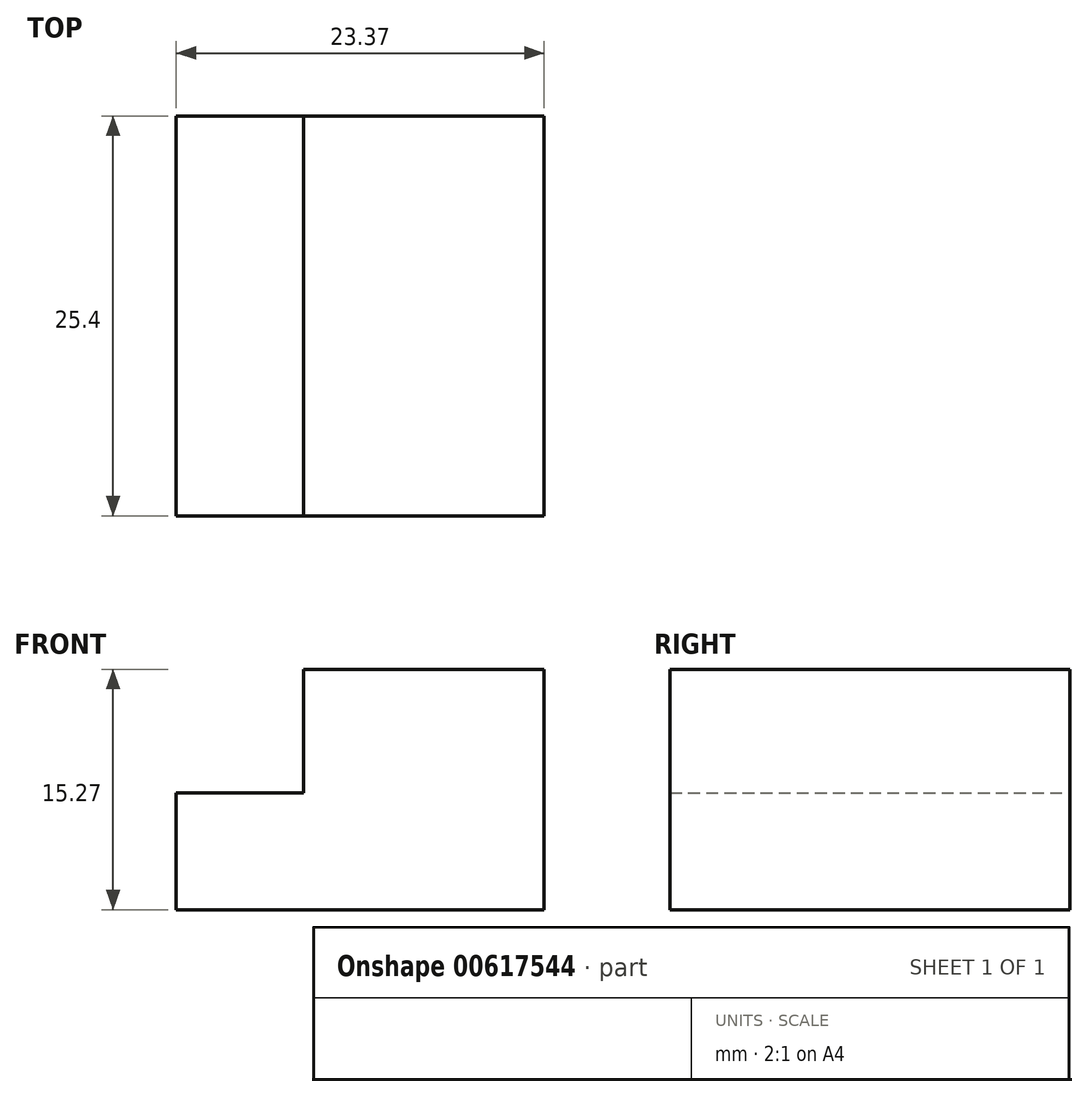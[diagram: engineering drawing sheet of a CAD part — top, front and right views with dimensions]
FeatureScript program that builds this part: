
annotation { "Feature Type Name" : "Feature", "Feature Type Description" : "" }
export const myFeature = defineFeature(function(context is Context, id is Id, definition is map)
    precondition{}
    {
        {
            var Q0;
            Q0=qCreatedBy(makeId("Front.planeOp"),FACE);
            var sketch = newSketch(context, id + "F0", { "sketchPlane" : qUnion([Q0])});
            skLineSegment(sketch, "E0", {"start": v(23.37, 0) * mm, "end": v(23.37, 15.27) * mm});
            skLineSegment(sketch, "E1", {"start": v(23.37, 15.27) * mm, "end": v(8.1, 15.27) * mm});
            skLineSegment(sketch, "E2", {"start": v(8.1, 15.27) * mm, "end": v(8.1, 7.4) * mm});
            skLineSegment(sketch, "E3", {"start": v(8.1, 7.4) * mm, "end": v(0, 7.4) * mm});
            skLineSegment(sketch, "E4", {"start": v(0, 7.4) * mm, "end": v(0, 0) * mm});
            skLineSegment(sketch, "E5", {"start": v(0, 0) * mm, "end": v(23.37, 0) * mm});
            skSolve(sketch);
        }
        {
            var Q0;
            Q0 = qSketchRegion(id + "F0", true);
            extrude(context, id + "F1", {"entities" : qUnion([Q0]), "depth" : 25.4 * mm, "offsetDistance" : 25.4 * mm});
        }
    });
